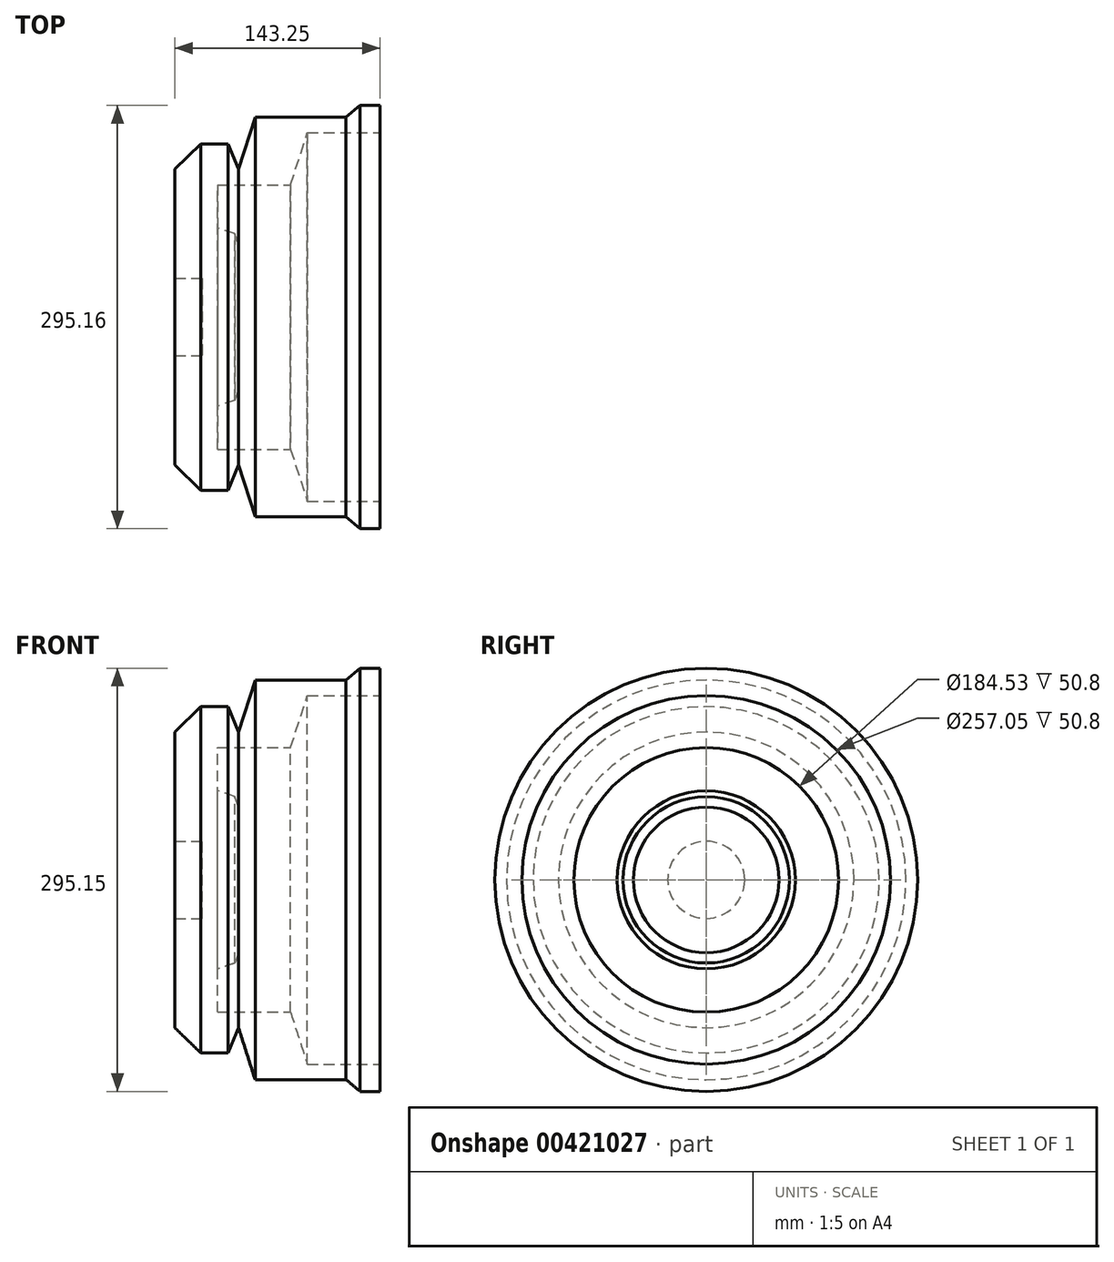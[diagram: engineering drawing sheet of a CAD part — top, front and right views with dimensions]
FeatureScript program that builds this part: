
annotation { "Feature Type Name" : "Feature", "Feature Type Description" : "" }
export const myFeature = defineFeature(function(context is Context, id is Id, definition is map)
    precondition{}
    {
        {
            var Q0;
            Q0=qCreatedBy(makeId("Front.planeOp"),FACE);
            var sketch = newSketch(context, id + "F0", { "sketchPlane" : qUnion([Q0])});
            skLineSegment(sketch, "E0", {"start": v(-44.45, 20.12) * mm, "end": v(-26.2, 37.78) * mm});
            skLineSegment(sketch, "E1", {"start": v(-26.2, 37.78) * mm, "end": v(-7.14, 37.78) * mm});
            skLineSegment(sketch, "E2", {"start": v(-7.14, 37.78) * mm, "end": v(0, 20.12) * mm});
            skLineSegment(sketch, "E3", {"start": v(0, 20.12) * mm, "end": v(11.6, 56.4) * mm});
            skLineSegment(sketch, "E4", {"start": v(11.6, 56.4) * mm, "end": v(37, 56.4) * mm});
            skLineSegment(sketch, "E5", {"start": v(37, 56.4) * mm, "end": v(75.1, 56.4) * mm});
            skLineSegment(sketch, "E6", {"start": v(75.1, 56.4) * mm, "end": v(84.83, 64.57) * mm});
            skLineSegment(sketch, "E7", {"start": v(84.83, 64.57) * mm, "end": v(98.8, 64.57) * mm});
            skLineSegment(sketch, "E8", {"start": v(98.8, 64.57) * mm, "end": v(98.8, 45.52) * mm});
            skLineSegment(sketch, "E9", {"start": v(98.8, 45.52) * mm, "end": v(48, 45.52) * mm});
            skLineSegment(sketch, "E10", {"start": v(48, 45.52) * mm, "end": v(36.3, 9.26) * mm});
            skLineSegment(sketch, "E11", {"start": v(36.3, 9.26) * mm, "end": v(-14.5, 9.26) * mm});
            skLineSegment(sketch, "E12", {"start": v(-14.5, 9.26) * mm, "end": v(-14.5, -20.89) * mm});
            skLineSegment(sketch, "E13", {"start": v(-14.5, -20.89) * mm, "end": v(-2.48, -25) * mm});
            skLineSegment(sketch, "E14", {"start": v(-2.48, -25) * mm, "end": v(0, -32.2) * mm});
            skLineSegment(sketch, "E15", {"start": v(0, -32.2) * mm, "end": v(0, -83) * mm});
            skLineSegment(sketch, "E16", {"start": v(0, -83) * mm, "end": v(-25.4, -83) * mm});
            skLineSegment(sketch, "E17", {"start": v(-25.4, -83) * mm, "end": v(-25.4, -56.08) * mm});
            skLineSegment(sketch, "E18", {"start": v(-25.4, -56.08) * mm, "end": v(-44.45, -56.08) * mm});
            skLineSegment(sketch, "E19", {"start": v(-44.45, -56.08) * mm, "end": v(-44.45, 20.12) * mm});
            skSolve(sketch);
        }
        {
            var Q0;
            Q0=makeQuery(id+"F0.imprint","IMPRINT",FACE,{"disambiguationData":[TD([[makeQuery(id+"F0.imprint","IMPRINT",EDGE,{"derivedFrom":sQuery(id+"F0.wireOp",EDGE,"E0")}),-1.0]])]});
            var Q1;
            Q1=sQuery(id+"F0.wireOp",EDGE,"E16");
            revolve(context, id + "F1", {"entities" : qUnion([Q0]), "axis" : qUnion([Q1]), "revolveType" : RevolveType.FULL});
        }
    });
